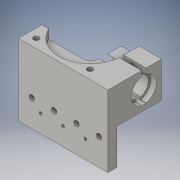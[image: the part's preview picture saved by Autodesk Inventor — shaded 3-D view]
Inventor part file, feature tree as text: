
AUTODESK INVENTOR PART (.ipt)
format: ipt  version: 2016 (Build 200138000, 138)  size: 332,800 bytes
history: native  units: mm
features: sketch x17, projected_geometry x17, extrude x10, hole x7, fillet x1
ambient origin geometry x8: Origin, YZ Plane, XZ Plane, XY Plane, X Axis, Y Axis, Z Axis, Center Point
bodies: Solid1 (feature_tree)
feature tree (52):
  extrude  "Extrusion1"  Depth=40.0mm
  extrude  "Extrusion2"  Depth=40.0mm
  extrude  "Extrusion3"  Depth=40.0mm
  hole  "Hole1"  [1 undecoded]
  hole  "Hole7"  [1 undecoded]
  extrude  "Extrusion10"  Depth=10.0mm
  extrude  "Extrusion11"  Depth=5.0mm TaperAngle=0.0deg
  extrude  "Extrusion15"  Depth=6.0mm
  extrude  "Extrusion16"  Depth=10.0mm TaperAngle=0.0deg
  fillet  "Fillet3"  Radius=15.0mm
  extrude  "Extrusion17"  Depth=10.0mm
  extrude  "Extrusion18"  Depth=40.0mm TaperAngle=0.0deg
  sketch  "Sketch27"  dims[d127=10.0mm d128=40.0mm d129=0.0mm]
  extrude  "Extrusion19"  Depth=10.0mm
  hole  "Hole9"  [1 undecoded]
  hole  "Hole10"  [1 undecoded]
  hole  "Hole11"  [1 undecoded]
  hole  "Hole12"  [1 undecoded]
  hole  "Hole13"  [1 undecoded]
  sketch  "Sketch1"  dims[d0=20.0mm d1=40.0mm]
  sketch  "Sketch2"  dims[d2=40.0mm d3=60.0mm]
  projected_geometry  "Projected Loop1"
  sketch  "Sketch3"  dims[d4=40.0mm d5=0.0mm d6=70.0mm]
  projected_geometry  "Projected Loop2"
  sketch  "Sketch6"  dims[d7=10.0mm d8=0.0mm d9=22.0mm]
  sketch  "Sketch16"  dims[d10=65.0mm d11=0.0mm d19=60.0mm]
  projected_geometry  "Projected Loop12"
  projected_geometry  "Projected Loop13"
  sketch  "Sketch18"  dims[d20=60.0mm]
  projected_geometry  "Projected Loop15"
  sketch  "Sketch19"  dims[d21=6.0mm d22=6.0mm d23=4.0mm d24=2.0mm d25=90.0deg d26=30.0mm d27=20.594885mm d86=10.0mm]
  projected_geometry  "Projected Loop16"
  sketch  "Sketch23"  dims[d87=2.156mm d88=5.69mm d89=7.5mm d90=4.0mm d91=90.0deg d92=8.865mm d93=20.594885mm d104=5.0mm d105=0.0mm]
  projected_geometry  "Projected Loop21"
  sketch  "Sketch24"  dims[d106=6.0mm d107=0.0mm d119=5.0mm]
  projected_geometry  "Projected Loop22"
  sketch  "Sketch25"  dims[d120=14.0mm d121=10.0mm d122=0.0mm d123=15.0mm]
  projected_geometry  "Projected Loop23"
  sketch  "Sketch26"  dims[d124=34.0mm d125=0.0mm d126=10.0mm]
  projected_geometry  "Projected Loop24"
  projected_geometry  "Projected Loop25"
  sketch  "Sketch28"  dims[d130=10.0mm d131=0.0mm d132=10.0mm]
  projected_geometry  "Projected Loop26"
  sketch  "Sketch29"  dims[d133=28.0mm d134=6.0mm d135=0.0mm]
  projected_geometry  "Projected Loop27"
  projected_geometry  "Projected Loop28"
  sketch  "Sketch30"  dims[d136=5.0mm d138=10.0mm]
  projected_geometry  "Projected Loop29"
  sketch  "Sketch31"  dims[d140=5.0mm d141=6.0mm d142=9.0mm d143=5.0mm d144=90.0deg d145=8.0mm d146=20.594885mm]
  projected_geometry  "Projected Loop30"
  sketch  "Sketch32"  dims[d147=4.134mm d148=10.0mm d149=10.5mm d150=6.0mm d151=90.0deg d152=14.2mm d153=20.594885mm d154=25.0mm d155=25.0mm d156=25.0mm d157=6.0mm d158=6.0mm d159=10.5mm d160=6.5mm d161=90.0deg d162=8.0mm d163=20.594885mm d164=20.0mm d165=25.0mm d166=25.0mm d167=3.242mm d168=8.0mm d169=10.5mm d170=6.5mm d171=90.0deg d172=10.0mm d173=20.594885mm d174=50.0mm d175=25.0mm d176=25.0mm d177=3.242mm d178=10.0mm d179=4.0mm d180=2.0mm d181=90.0deg d182=11.8mm d183=20.594885mm]
  projected_geometry  "Projected Loop31"
note: 7 required parameter values undecoded (feature->parameter linkage not recoverable at this tier; creation-order binding heuristic only, values carry confidence <= 0.55)
